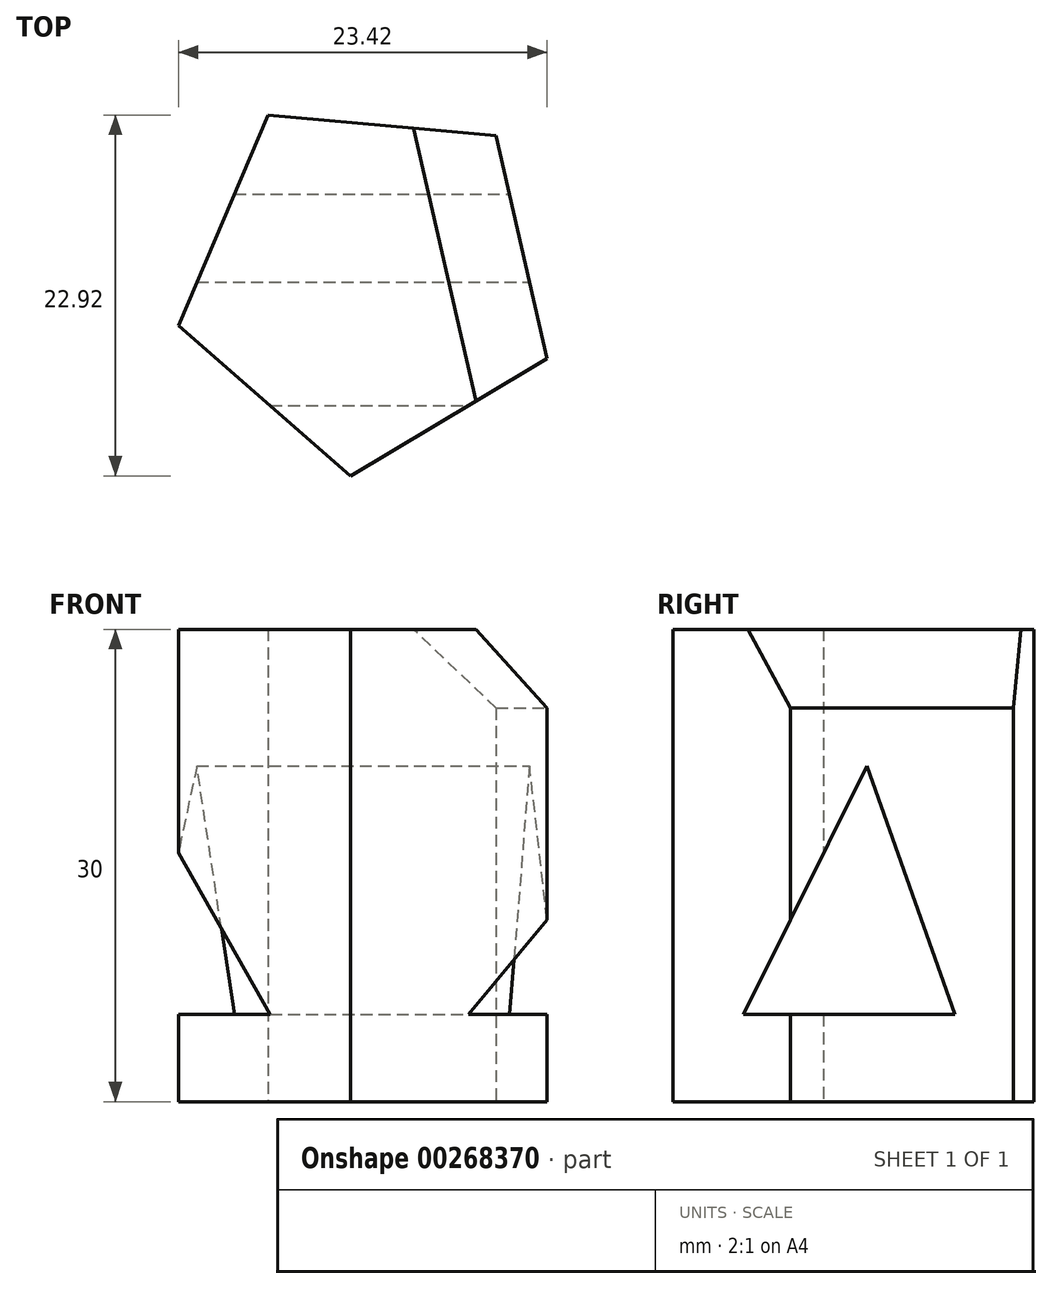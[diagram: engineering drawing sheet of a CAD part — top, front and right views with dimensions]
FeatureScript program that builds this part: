
annotation { "Feature Type Name" : "Feature", "Feature Type Description" : "" }
export const myFeature = defineFeature(function(context is Context, id is Id, definition is map)
    precondition{}
    {
        {
            var Q0;
            Q0=qCreatedBy(makeId("Top.planeOp"),FACE);
            var sketch = newSketch(context, id + "F0", { "sketchPlane" : qUnion([Q0])});
            skCircle(sketch, "E0.cCircle", {"center": v(0, 0) * mm, "radius": 10 * mm, "construction": true});
            skLineSegment(sketch, "E0.0", {"start": v(11.37, -4.86) * mm, "end": v(-1.1, -12.31) * mm});
            skLineSegment(sketch, "E0.1", {"start": v(-1.1, -12.31) * mm, "end": v(-12.05, -2.75) * mm});
            skLineSegment(sketch, "E0.2", {"start": v(-12.05, -2.75) * mm, "end": v(-6.34, 10.6) * mm});
            skLineSegment(sketch, "E0.3", {"start": v(-6.34, 10.6) * mm, "end": v(8.13, 9.31) * mm});
            skLineSegment(sketch, "E0.4", {"start": v(8.13, 9.31) * mm, "end": v(11.37, -4.86) * mm});
            skPoint(sketch, "E0.0.midPoint", {"position": v(5.13, -8.58) * mm});
            skSolve(sketch);
        }
        {
            var Q0;
            Q0=makeQuery(id+"F0.imprint","IMPRINT",FACE,{"disambiguationData":[TD([[makeQuery(id+"F0.imprint","IMPRINT",EDGE,{"derivedFrom":sQuery(id+"F0.wireOp",EDGE,"E0.0")}),-1.0]])]});
            extrude(context, id + "F1", {"entities" : qUnion([Q0]), "depth" : 30 * mm});
        }
        {
            var Q0;
            Q0=qCreatedBy(makeId("Right.planeOp"),FACE);
            var sketch = newSketch(context, id + "F2", { "sketchPlane" : qUnion([Q0])});
            skLineSegment(sketch, "E1", {"start": v(-7.84, 5.54) * mm, "end": v(5.6, 5.54) * mm});
            skLineSegment(sketch, "E2", {"start": v(5.6, 5.54) * mm, "end": v(0, 21.33) * mm});
            skLineSegment(sketch, "E3", {"start": v(0, 21.33) * mm, "end": v(-7.84, 5.54) * mm});
            skSolve(sketch);
        }
        {
            var Q0;
            Q0 = qSketchRegion(id + "F2", true);
            extrude(context, id + "F3", {"entities" : qUnion([Q0]), "operationType" : NewBodyOperationType.REMOVE, "endBound" : BoundingType.UP_TO_NEXT, "oppositeDirection" : true, "depth" : 25 * mm, "hasSecondDirection" : true, "secondDirectionBound" : SecondDirectionBoundingType.UP_TO_NEXT, "secondDirectionOppositeDirection" : false, "secondDirectionDepth" : 25 * mm});
        }
        {
            var Q0;
            Q0=makeQuery(id+"F1.opExtrude","CAP_EDGE",EDGE,{"disambiguationData":[OSD([sQuery(id+"F0.wireOp",EDGE,"E0.4")])],"isStart":false});
            chamfer(context, id + "F4", {"entities" : qUnion([Q0]), "width" : 5 * mm, "tangentPropagation" : true});
        }
    });
